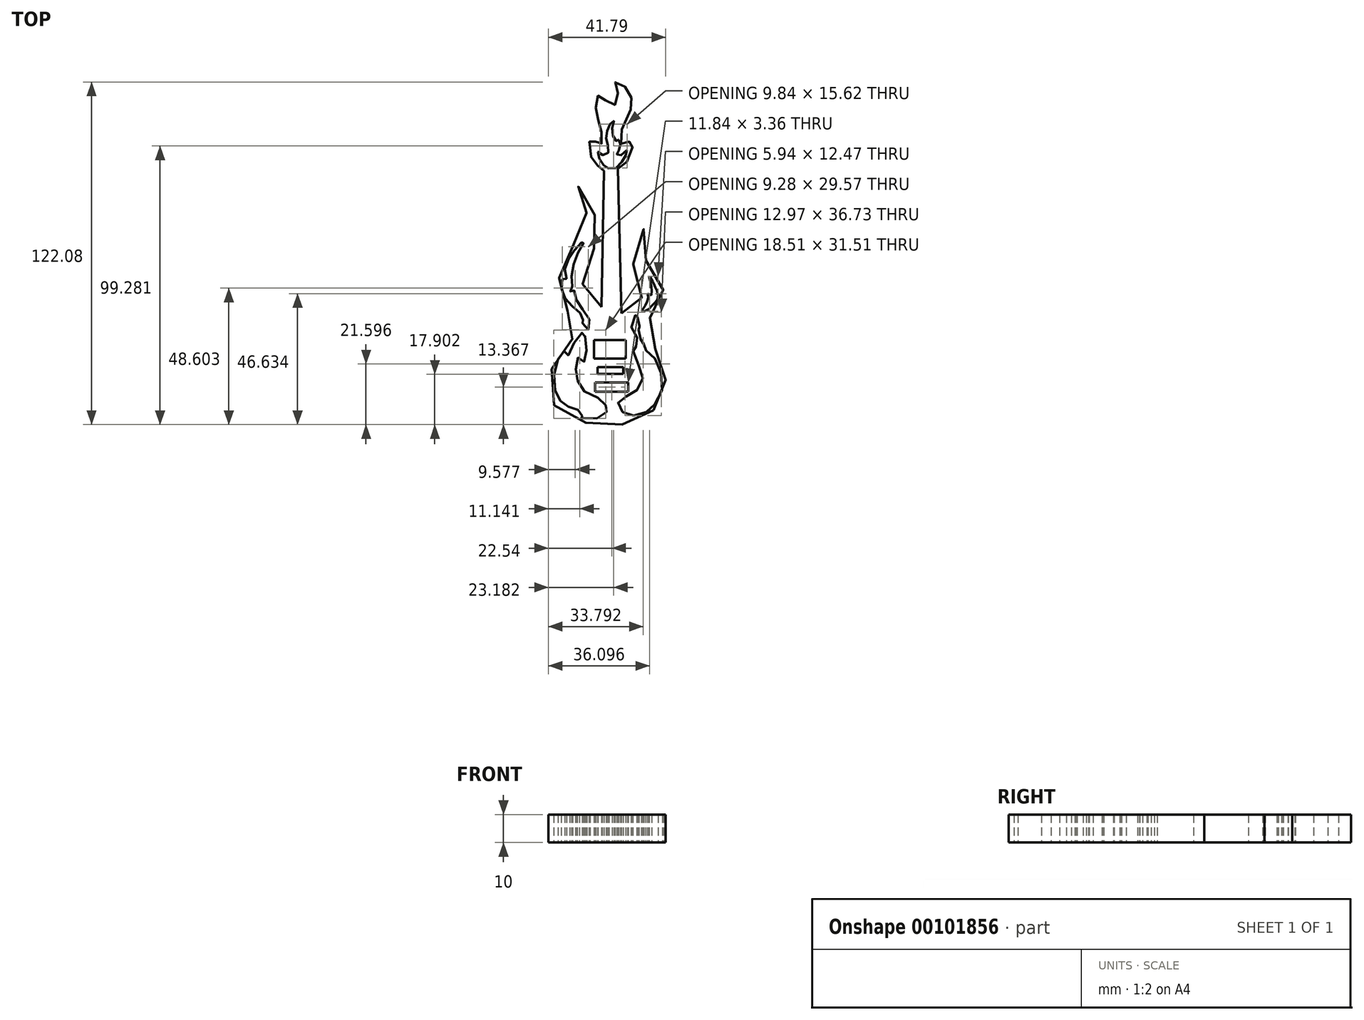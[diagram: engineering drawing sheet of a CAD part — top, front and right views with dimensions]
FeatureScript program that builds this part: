
annotation { "Feature Type Name" : "Feature", "Feature Type Description" : "" }
export const myFeature = defineFeature(function(context is Context, id is Id, definition is map)
    precondition{}
    {
        {
            var Q0;
            Q0=qCreatedBy(makeId("Top.planeOp"),FACE);
            var sketch = newSketch(context, id + "F0", { "sketchPlane" : qUnion([Q0])});
            skFitSpline(sketch, "E0", {"points": [v(-3.35, -3.12) * mm, v(-7.77, 0) * mm, v(-10.24, 6.78) * mm, v(-6.88, 15.8) * mm, v(-4.58, 23.4) * mm, v(-6.18, 31) * mm, v(-9.18, 37.18) * mm, v(-12.62, 40.34) * mm, v(-9.2, 32.23) * mm, v(-9.6, 24.3) * mm, v(-14.7, 17.33) * mm, v(-18.02, 9.08) * mm, v(-18.37, 0) * mm, v(-14.3, -6.12) * mm, v(-12.36, -11.96) * mm, v(-16.43, -17.44) * mm, v(-21.2, -25.21) * mm, v(-21.9, -34.23) * mm, v(-16.78, -41.83) * mm, v(-8.47, -44.48) * mm, v(0, -45) * mm, v(8.85, -44.12) * mm, v(15.21, -39.88) * mm, v(18.57, -34.93) * mm, v(19.28, -25.74) * mm, v(16.8, -19.56) * mm, v(13.62, -14.08) * mm, v(13.97, -6.83) * mm, v(18.4, -1.7) * mm, v(17.5, 6.07) * mm, v(13.44, 11.9) * mm, v(11.15, 19.86) * mm, v(11.65, 24.63) * mm, v(7.23, 15.8) * mm, v(10.44, 7.84) * mm, v(10.97, 0) * mm, v(7.47, -4.17) * mm, v(3.72, -5.42) * mm], "startDerivative": vector(-203.42, 108.23) * mm, "endDerivative": vector(-182.4, -44.2) * mm});
            skFitSpline(sketch, "E1", {"points": [v(2.5, 46.16) * mm, v(6.4, 49.86) * mm, v(7.47, 56.05) * mm, v(4.11, 54.64) * mm, v(3.95, 60.47) * mm, v(6.07, 64.7) * mm, v(7.32, 69.3) * mm, v(5.74, 74.6) * mm, v(1.5, 76.91) * mm, v(2.73, 71.26) * mm, v(0, 68.79) * mm, v(-3.99, 72.5) * mm, v(-5.4, 68.8) * mm, v(-4.18, 62.43) * mm, v(-3.13, 56.95) * mm, v(-4.02, 54.48) * mm, v(-7.02, 56.96) * mm, v(-7.2, 50.77) * mm, v(-4.56, 47.06) * mm, v(-2.45, 45.46) * mm, v(2.5, 46.16) * mm]});
            skLineSegment(sketch, "E2", {"start": v(-2.45, 45.46) * mm, "end": v(-3.35, -3.12) * mm});
            skLineSegment(sketch, "E3", {"start": v(2.5, 46.16) * mm, "end": v(3.72, -5.42) * mm});
            skLineSegment(sketch, "E4", {"start": v(-3.35, -3.12) * mm, "end": v(-3.35, -12.84) * mm});
            skLineSegment(sketch, "E5", {"start": v(-3.35, -12.84) * mm, "end": v(3.72, -12.84) * mm});
            skLineSegment(sketch, "E6", {"start": v(3.72, -12.84) * mm, "end": v(3.72, -5.42) * mm});
            skLineSegment(sketch, "E7.bottom", {"start": v(-6.02, -14.96) * mm, "end": v(5.29, -14.96) * mm});
            skLineSegment(sketch, "E7.top", {"start": v(-6.02, -21.5) * mm, "end": v(5.29, -21.5) * mm});
            skLineSegment(sketch, "E7.left", {"start": v(-6.02, -14.96) * mm, "end": v(-6.02, -21.5) * mm});
            skLineSegment(sketch, "E7.right", {"start": v(5.29, -14.96) * mm, "end": v(5.29, -21.5) * mm});
            skLineSegment(sketch, "E8.bottom", {"start": v(-4.79, -24.5) * mm, "end": v(4.43, -24.5) * mm});
            skLineSegment(sketch, "E8.top", {"start": v(-4.79, -26.93) * mm, "end": v(4.43, -26.93) * mm});
            skLineSegment(sketch, "E8.left", {"start": v(-4.79, -24.5) * mm, "end": v(-4.79, -26.93) * mm});
            skLineSegment(sketch, "E8.right", {"start": v(4.43, -24.5) * mm, "end": v(4.43, -26.93) * mm});
            skLineSegment(sketch, "E9.bottom", {"start": v(-5.67, -29.98) * mm, "end": v(6.17, -29.98) * mm});
            skLineSegment(sketch, "E9.top", {"start": v(-5.67, -33.34) * mm, "end": v(6.17, -33.34) * mm});
            skLineSegment(sketch, "E9.left", {"start": v(-5.67, -29.98) * mm, "end": v(-5.67, -33.34) * mm});
            skLineSegment(sketch, "E9.right", {"start": v(6.17, -29.98) * mm, "end": v(6.17, -33.34) * mm});
            skFitSpline(sketch, "E10", {"points": [v(-1.9, -38.18) * mm, v(-3.45, -36.09) * mm, v(-7.98, -34.42) * mm, v(-11.28, -30.73) * mm, v(-12.18, -28.27) * mm, v(-12.57, -24.77) * mm, v(-11.86, -21.39) * mm, v(-10.83, -20.76) * mm, v(-9.47, -22.7) * mm, v(-8.75, -19.14) * mm, v(-8.95, -14.61) * mm, v(-9.98, -11.37) * mm, v(-10.76, -13.64) * mm, v(-13.6, -16.55) * mm, v(-15.3, -20.57) * mm, v(-15.94, -20.94) * mm, v(-16.98, -18.5) * mm, v(-18.72, -21.45) * mm, v(-20.28, -27.5) * mm, v(-19.76, -33.26) * mm, v(-18.01, -36.41) * mm, v(-17.82, -37.01) * mm, v(-15.16, -38.7) * mm, v(-13.6, -39.47) * mm, v(-10.24, -40.38) * mm, v(-9.98, -41.87) * mm, v(-11.93, -42.19) * mm, v(-8.5, -43.1) * mm, v(-3.9, -42.38) * mm, v(-1.5, -40.44) * mm, v(-1.24, -39.08) * mm, v(-1.9, -38.18) * mm]});
            skFitSpline(sketch, "E11", {"points": [v(8.01, -41.8) * mm, v(11.7, -40.96) * mm, v(13.9, -39.66) * mm, v(15.85, -37.53) * mm, v(18.18, -32.8) * mm, v(17.85, -26.78) * mm, v(16.1, -22.06) * mm, v(13.9, -19.73) * mm, v(11.57, -17.72) * mm, v(11, -16.36) * mm, v(12.42, -16.62) * mm, v(11.12, -15.32) * mm, v(10.02, -13.38) * mm, v(9.76, -11.18) * mm, v(11.19, -11.83) * mm, v(10.02, -9.82) * mm, v(9.24, -7.49) * mm, v(9.5, -6.26) * mm, v(9.57, -4.96) * mm, v(8.08, -7.17) * mm, v(7.24, -10.01) * mm, v(8.27, -12.73) * mm, v(9.9, -15.2) * mm, v(9.24, -17.4) * mm, v(7.95, -16.36) * mm, v(8.01, -19.4) * mm, v(9.63, -23.48) * mm, v(11.25, -27.1) * mm, v(10.8, -30.93) * mm, v(8.6, -33.32) * mm, v(5.81, -34.87) * mm, v(3.55, -35.9) * mm, v(2.51, -37.72) * mm, v(3.48, -40.12) * mm, v(5.3, -41.09) * mm, v(8.01, -41.8) * mm]});
            skFitSpline(sketch, "E12", {"points": [v(-8.07, -11.21) * mm, v(-7.46, -9.2) * mm, v(-8.48, -6.06) * mm, v(-10.78, -3.2) * mm, v(-12.24, -0.96) * mm, v(-12.8, 1.95) * mm, v(-13.18, 2.7) * mm, v(-13.7, 1.52) * mm, v(-14.64, 3.05) * mm, v(-14.39, 4.63) * mm, v(-13.73, 4.28) * mm, v(-13.9, 6.38) * mm, v(-13.75, 9.82) * mm, v(-12.76, 13.62) * mm, v(-11.56, 16.44) * mm, v(-10.36, 18.62) * mm, v(-9.15, 20.82) * mm, v(-10.63, 19.72) * mm, v(-12.45, 17.69) * mm, v(-13.7, 16.12) * mm, v(-15.16, 13.73) * mm, v(-16.3, 11.12) * mm, v(-16.15, 8.36) * mm, v(-15.82, 6.75) * mm, v(-16.46, 5.74) * mm, v(-17.4, 6.87) * mm, v(-17.71, 4.46) * mm, v(-17.14, 1.9) * mm, v(-15.94, -0.6) * mm, v(-14.17, -2.42) * mm, v(-12.19, -4.4) * mm, v(-10.42, -5.91) * mm, v(-9.55, -7.64) * mm, v(-11.1, -7.56) * mm, v(-10.62, -8.61) * mm, v(-8.95, -9.74) * mm, v(-8.07, -11.21) * mm]});
            skFitSpline(sketch, "E13", {"points": [v(10.84, -4.63) * mm, v(12.84, -4.35) * mm, v(14.86, -2.37) * mm, v(16.37, -0.71) * mm, v(16.72, 1.55) * mm, v(15.86, 3.88) * mm, v(15.67, 4.2) * mm, v(14.7, 6.33) * mm, v(13.65, 7.84) * mm, v(14.22, 5.13) * mm, v(14.53, 2.48) * mm, v(14.17, 0.97) * mm, v(13.18, 1.74) * mm, v(13.26, 0.44) * mm, v(12.77, -1.45) * mm, v(11.7, -3.52) * mm, v(10.84, -4.63) * mm]});
            skFitSpline(sketch, "E14", {"points": [v(1.85, 46.44) * mm, v(3.3, 47.95) * mm, v(4.68, 49.67) * mm, v(5.48, 51.36) * mm, v(5.87, 52.85) * mm, v(4.9, 51.93) * mm, v(3.56, 50.9) * mm, v(2.66, 50.6) * mm, v(2.1, 51.27) * mm, v(2.45, 52.7) * mm, v(2.68, 52.69) * mm, v(3.53, 53.85) * mm, v(3.4, 54.82) * mm, v(2.76, 55.44) * mm, v(2.77, 56.01) * mm, v(2.34, 57.15) * mm, v(2, 56.17) * mm, v(1.43, 56.27) * mm, v(0.78, 57.73) * mm, v(0.45, 59.52) * mm, v(0.6, 61.6) * mm, v(0.99, 63.05) * mm, v(1.09, 63.6) * mm, v(-0.56, 61.72) * mm, v(-1.2, 60.3) * mm, v(-1.7, 58.1) * mm, v(-1.67, 56.84) * mm, v(-1.38, 55.25) * mm, v(-0.75, 53.55) * mm, v(-0.99, 51.8) * mm, v(-2.04, 51.11) * mm, v(-3.26, 51.18) * mm, v(-4.2, 51.93) * mm, v(-4.68, 52.15) * mm, v(-4.42, 50.44) * mm, v(-3.53, 48.62) * mm, v(-2.3, 46.96) * mm, v(-1.57, 46.4) * mm, v(-0.39, 46.37) * mm, v(1.85, 46.44) * mm]});
            skSolve(sketch);
        }
        {
            var Q0;
            Q0=qSketchRegion(id+"F0",true);
            extrude(context, id + "F1", {"entities" : qUnion([Q0]), "depth" : 10 * mm});
        }
    });
